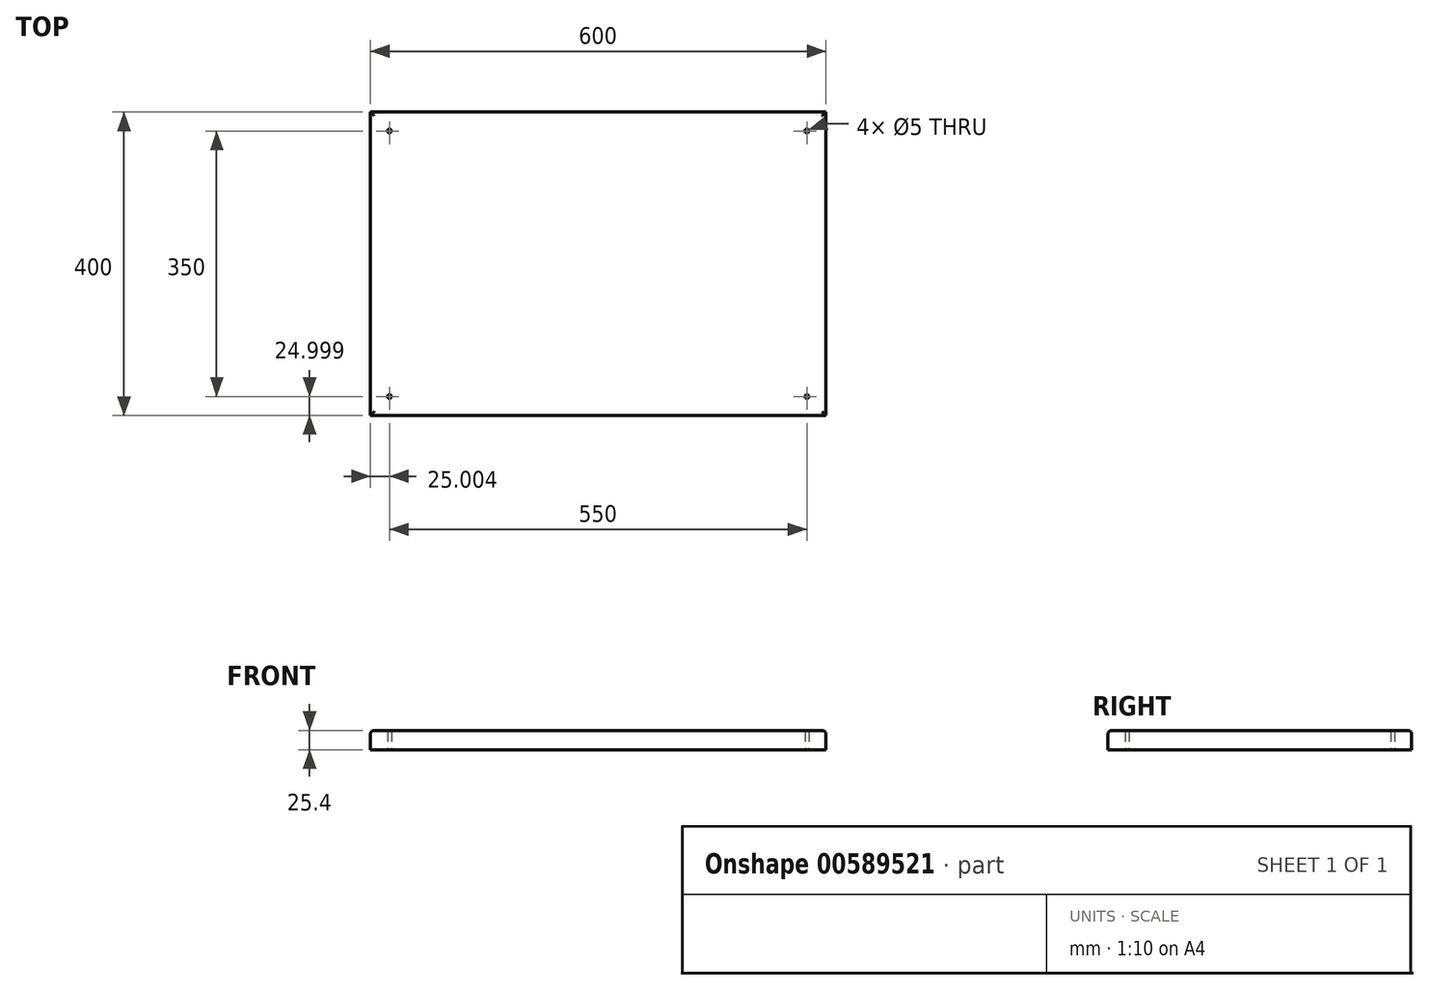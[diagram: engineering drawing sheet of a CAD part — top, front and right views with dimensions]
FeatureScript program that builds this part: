
annotation { "Feature Type Name" : "Feature", "Feature Type Description" : "" }
export const myFeature = defineFeature(function(context is Context, id is Id, definition is map)
    precondition{}
    {
        {
            var Q0;
            Q0=qCreatedBy(makeId("Top.planeOp"),FACE);
            var sketch = newSketch(context, id + "F0", { "sketchPlane" : qUnion([Q0])});
            skLineSegment(sketch, "E0.bottom", {"start": v(-298.13, 211.68) * mm, "end": v(301.87, 211.68) * mm});
            skLineSegment(sketch, "E0.top", {"start": v(-298.13, -188.32) * mm, "end": v(301.87, -188.32) * mm});
            skLineSegment(sketch, "E0.left", {"start": v(-298.13, 211.68) * mm, "end": v(-298.13, -188.32) * mm});
            skLineSegment(sketch, "E0.right", {"start": v(301.87, 211.68) * mm, "end": v(301.87, -188.32) * mm});
            skCircle(sketch, "E1", {"center": v(-273.13, -163.32) * mm, "radius": 2.5 * mm});
            skCircle(sketch, "E2", {"center": v(276.87, -163.32) * mm, "radius": 2.5 * mm});
            skCircle(sketch, "E3", {"center": v(276.87, 186.68) * mm, "radius": 2.5 * mm});
            skCircle(sketch, "E4", {"center": v(-273.13, 186.68) * mm, "radius": 2.5 * mm});
            skSolve(sketch);
        }
        {
            var Q0;
            Q0=makeQuery(id+"F0.imprint","IMPRINT",FACE,{"disambiguationData":[TD([[makeQuery(id+"F0.imprint","IMPRINT",EDGE,{"derivedFrom":sQuery(id+"F0.wireOp",EDGE,"E0.bottom")}),-1.0]])]});
            extrude(context, id + "F1", {"entities" : qUnion([Q0]), "depth" : 25.4 * mm, "offsetDistance" : 25.4 * mm});
        }
        {
            var Q0;
            Q0=makeQuery(id+"F1.opExtrude","CAP_EDGE",EDGE,{"disambiguationData":[OSD([sQuery(id+"F0.wireOp",EDGE,"E0.top")])],"isStart":false});
            var Q1;
            Q1=makeQuery(id+"F1.opExtrude","CAP_EDGE",EDGE,{"disambiguationData":[OSD([sQuery(id+"F0.wireOp",EDGE,"E0.left")])],"isStart":false});
            var Q2;
            Q2=makeQuery(id+"F1.opExtrude","CAP_EDGE",EDGE,{"disambiguationData":[OSD([sQuery(id+"F0.wireOp",EDGE,"E0.bottom")])],"isStart":false});
            var Q3;
            Q3=makeQuery(id+"F1.opExtrude","CAP_EDGE",EDGE,{"disambiguationData":[OSD([sQuery(id+"F0.wireOp",EDGE,"E0.right")])],"isStart":false});
            fillet(context, id + "F2", {"entities" : qUnion([Q0, Q1, Q2, Q3]), "radius" : 5 * mm, "tangentPropagation" : true, "allowEdgeOverflow" : false});
        }
    });
